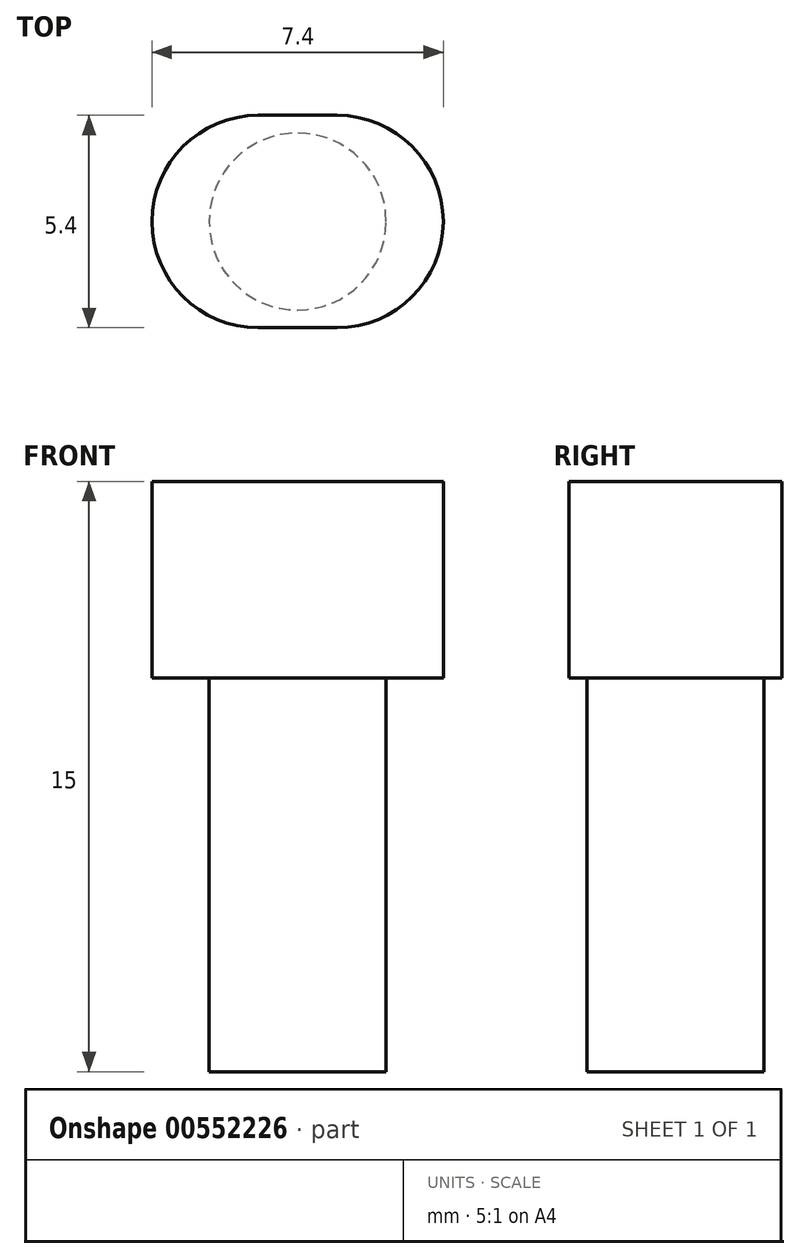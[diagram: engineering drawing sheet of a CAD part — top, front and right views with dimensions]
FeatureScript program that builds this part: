
annotation { "Feature Type Name" : "Feature", "Feature Type Description" : "" }
export const myFeature = defineFeature(function(context is Context, id is Id, definition is map)
    precondition{}
    {
        {
            var Q0;
            Q0=qCreatedBy(makeId("Top.planeOp"),FACE);
            var sketch = newSketch(context, id + "F0", { "sketchPlane" : qUnion([Q0])});
            skLineSegment(sketch, "E0", {"start": v(0, 0) * mm, "end": v(-1, 0) * mm, "construction": true});
            skArc(sketch, "E1", {"start": v(-1, 2.7) * mm, "mid": v(-3.7, 0) * mm, "end": v(-1, -2.7) * mm});
            skLineSegment(sketch, "E2", {"start": v(-1, 2.7) * mm, "end": v(1, 2.7) * mm});
            skLineSegment(sketch, "E3", {"start": v(-1, -2.7) * mm, "end": v(1, -2.7) * mm});
            skArc(sketch, "E4", {"start": v(1, -2.7) * mm, "mid": v(3.7, 0) * mm, "end": v(1, 2.7) * mm});
            skPoint(sketch, "E4.centerSnap0", {"position": v(-0.5, 0) * mm});
            skLineSegment(sketch, "E5", {"start": v(-1, 0) * mm, "end": v(-3.7, 0) * mm, "construction": true});
            skLineSegment(sketch, "E6", {"start": v(0, 0) * mm, "end": v(3.7, 0) * mm, "construction": true});
            skSolve(sketch);
        }
        {
            var Q0;
            Q0 = qSketchRegion(id + "F0", true);
            extrude(context, id + "F1", {"entities" : qUnion([Q0]), "depth" : 5 * mm, "offsetDistance" : 25 * mm});
        }
        {
            var Q0;
            Q0=makeQuery(id+"F1.opExtrude","CAP_FACE",FACE,{"disambiguationData":[OSD([sQuery(id+"F0.wireOp",EDGE,"E1"),sQuery(id+"F0.wireOp",EDGE,"E2"),sQuery(id+"F0.wireOp",EDGE,"E3"),sQuery(id+"F0.wireOp",EDGE,"E4")])],"isStart":true});
            var sketch = newSketch(context, id + "F2", { "sketchPlane" : qUnion([Q0])});
            skCircle(sketch, "E7", {"center": v(0, 0) * mm, "radius": 2.25 * mm});
            skSolve(sketch);
        }
        {
            var Q0;
            Q0 = qSketchRegion(id + "F2", true);
            extrude(context, id + "F3", {"entities" : qUnion([Q0]), "operationType" : NewBodyOperationType.ADD, "depth" : 10 * mm, "offsetDistance" : 25 * mm});
        }
    });
